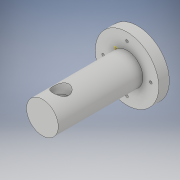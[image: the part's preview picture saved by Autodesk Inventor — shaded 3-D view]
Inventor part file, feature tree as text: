
AUTODESK INVENTOR PART (.ipt)
format: ipt  version: 2019 (Build 230136000, 136)  size: 145,408 bytes
history: native  units: in
note: dims shown in document units (in); Inventor stores cm internally (conversion verified against a paired STEP export)
features: extrude x6, sketch x6, plane x2
ambient origin geometry x8: Origin, YZ Plane, XZ Plane, XY Plane, X Axis, Y Axis, Z Axis, Center Point
bodies: Solid1 (feature_tree)
feature tree (14):
  plane  "Work Plane6"
  extrude  "Extrusion4"  Depth=4.0in TaperAngle=0.0deg
  plane  "Work Plane2"
  extrude  "Extrusion5"  Depth=0.25in TaperAngle=0.0deg
  extrude  "Extrusion6"  Depth=0.5in TaperAngle=0.0deg
  extrude  "Extrusion11"  Depth=1.5in TaperAngle=0.0deg
  extrude  "Extrusion12"  Depth=0.125in
  extrude  "Extrusion13"  Depth=0.125in
  sketch  "Sketch4"  dims[d11=2.0in d12=4.0in d13=0.0in]
  sketch  "Sketch5"  dims[d19=4.0in d20=0.0in d21=0.25in d22=0.0in]
  sketch  "Sketch6"  dims[d36=3.0in d37=0.5in d38=0.0in]
  sketch  "Sketch13"  dims[d39=1.5in d40=4.0in d41=0.0in]
  sketch  "Sketch14"  dims[d42=0.125in d43=0.125in]
  sketch  "Sketch15"  dims[d44=0.125in d45=0.125in d46=4.0in d47=0.0in]
